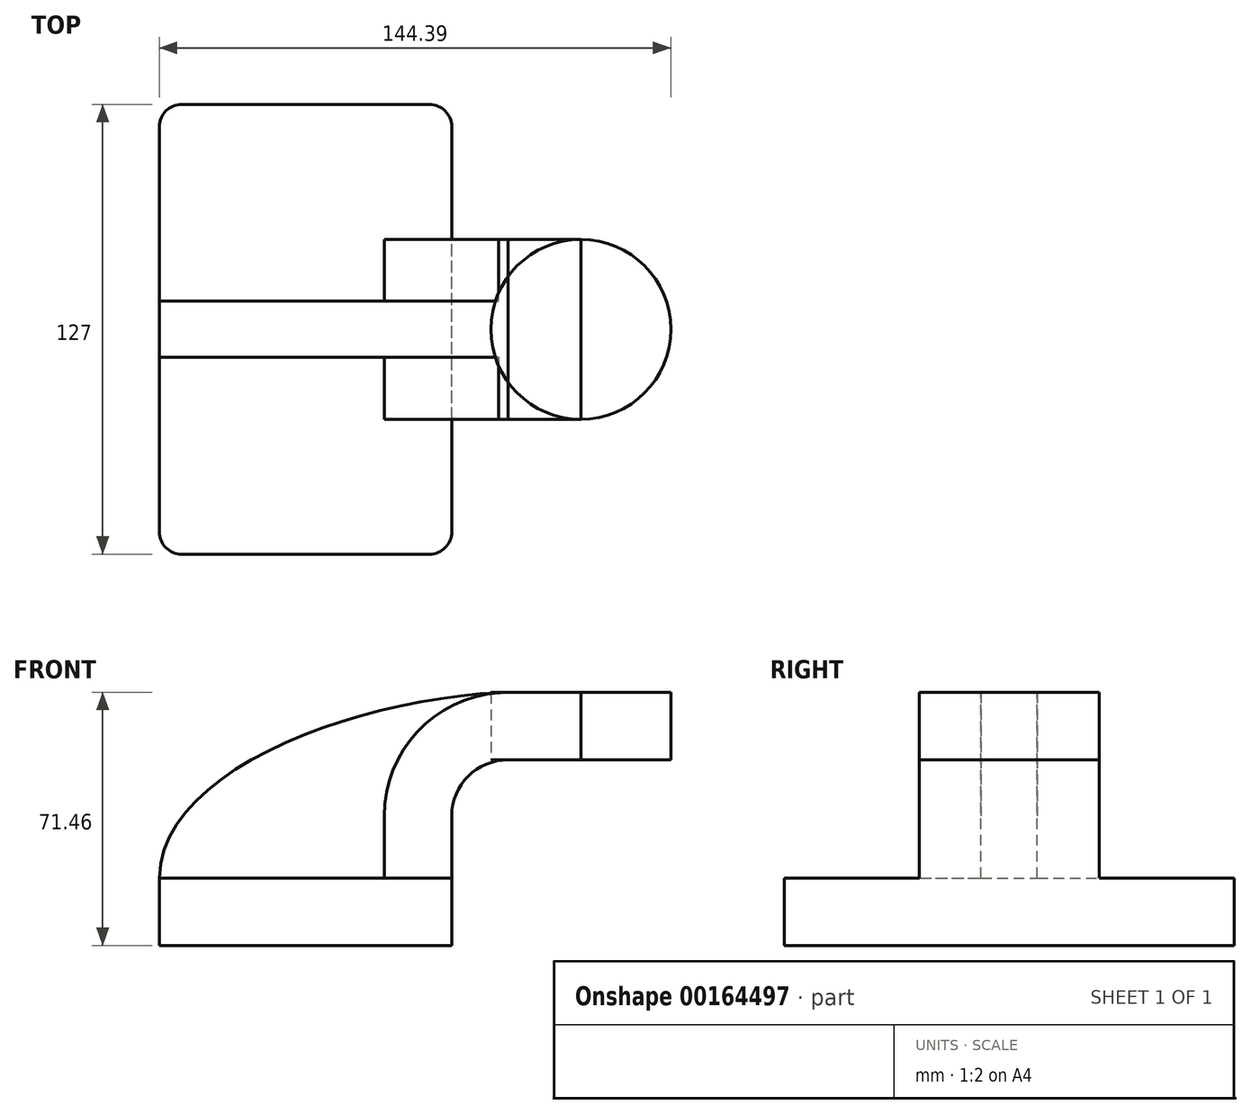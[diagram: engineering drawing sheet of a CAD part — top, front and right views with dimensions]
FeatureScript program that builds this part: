
annotation { "Feature Type Name" : "Feature", "Feature Type Description" : "" }
export const myFeature = defineFeature(function(context is Context, id is Id, definition is map)
    precondition{}
    {
        {
            var Q0;
            Q0=qCreatedBy(makeId("Front.planeOp"),FACE);
            var sketch = newSketch(context, id + "F0", { "sketchPlane" : qUnion([Q0])});
            skLineSegment(sketch, "E0.bottom", {"start": v(41.28, -9.52) * mm, "end": v(-41.28, -9.53) * mm});
            skLineSegment(sketch, "E0.top", {"start": v(41.28, 9.53) * mm, "end": v(-41.28, 9.53) * mm});
            skLineSegment(sketch, "E0.left", {"start": v(41.28, -9.52) * mm, "end": v(41.28, 9.53) * mm});
            skLineSegment(sketch, "E0.right", {"start": v(-41.28, -9.53) * mm, "end": v(-41.28, 9.53) * mm});
            skPoint(sketch, "E0.middle", {"position": v(0, 0) * mm});
            skLineSegment(sketch, "E1.bottom", {"start": v(128.51, 38.1) * mm, "end": v(77.71, 38.1) * mm});
            skLineSegment(sketch, "E1.top", {"start": v(128.51, 66.68) * mm, "end": v(77.71, 66.68) * mm});
            skLineSegment(sketch, "E1.left", {"start": v(128.51, 38.1) * mm, "end": v(128.51, 66.68) * mm});
            skLineSegment(sketch, "E1.right", {"start": v(77.71, 38.1) * mm, "end": v(77.71, 66.68) * mm});
            skPoint(sketch, "E1.middle", {"position": v(103.11, 52.39) * mm});
            skLineSegment(sketch, "E2", {"start": v(41.28, 9.53) * mm, "end": v(41.28, 27) * mm});
            skArc(sketch, "E3", {"start": v(41.27, 27) * mm, "mid": v(45.92, 38.23) * mm, "end": v(57.15, 42.88) * mm});
            skLineSegment(sketch, "E4", {"start": v(57.15, 42.88) * mm, "end": v(103.11, 42.88) * mm});
            skPoint(sketch, "E4.endSnap0", {"position": v(103.11, 38.1) * mm});
            skLineSegment(sketch, "E5.0", {"start": v(57.15, 61.93) * mm, "end": v(103.11, 61.93) * mm});
            skArc(sketch, "E5.1", {"start": v(22.23, 27) * mm, "mid": v(32.45, 51.7) * mm, "end": v(57.15, 61.93) * mm});
            skLineSegment(sketch, "E5.2", {"start": v(22.22, 9.53) * mm, "end": v(22.22, 27) * mm});
            skLineSegment(sketch, "E6", {"start": v(103.11, 42.88) * mm, "end": v(103.11, 61.93) * mm});
            skFitSpline(sketch, "E7", {"points": [v(-41.28, 9.53) * mm, v(57.15, 61.93) * mm], "startDerivative": vector(1.48, 94.5) * mm, "endDerivative": vector(120.77, 3.4) * mm});
            skSolve(sketch);
        }
        {
            var Q0;
            Q0=makeQuery(id+"F0.imprint","IMPRINT",FACE,{"disambiguationData":[TD([[makeQuery(id+"F0.imprint","IMPRINT",EDGE,{"derivedFrom":sQuery(id+"F0.wireOp",EDGE,"E0.bottom")}),-1.0]])]});
            extrude(context, id + "F1", {"entities" : qUnion([Q0]), "endBound" : BoundingType.SYMMETRIC, "depth" : 127 * mm});
        }
        {
            var Q0;
            {var subQ1=sQuery(id+"F0.wireOp",EDGE,"E2");Q0=makeQuery(id+"F0.imprint","IMPRINT",FACE,{"disambiguationData":[TD([[makeQuery(id+"F0.imprint","IMPRINT",EDGE,{"derivedFrom":subQ1}),1.0]])]});}
            extrude(context, id + "F2", {"entities" : qUnion([Q0]), "operationType" : NewBodyOperationType.ADD, "endBound" : BoundingType.SYMMETRIC, "depth" : 50.8 * mm});
        }
        {
            var Q0;
            {var subQ3=sQuery(id+"F0.wireOp",EDGE,"E5.2");Q0=makeQuery(id+"F0.imprint","IMPRINT",FACE,{"disambiguationData":[TD([[makeQuery(id+"F0.imprint","IMPRINT",EDGE,{"derivedFrom":subQ3}),1.0]])]});}
            extrude(context, id + "F3", {"entities" : qUnion([Q0]), "operationType" : NewBodyOperationType.ADD, "endBound" : BoundingType.SYMMETRIC, "depth" : 15.88 * mm});
        }
        {
            var Q0;
            {var subQ5=sQuery(id+"F0.wireOp",EDGE,"E6");Q0=makeQuery(id+"F0.imprint","IMPRINT",FACE,{"disambiguationData":[TD([[makeQuery(id+"F0.imprint","IMPRINT",EDGE,{"derivedFrom":subQ5}),1.0]])]});}
            var Q1;
            Q1=sQuery(id+"F0.wireOp",EDGE,"E1.right");
            revolve(context, id + "F4", {"entities" : qUnion([Q0]), "axis" : qUnion([Q1]), "revolveType" : RevolveType.FULL});
        }
        {
            var Q0;
            Q0=makeQuery(id+"F1.opExtrude","CAP_EDGE",EDGE,{"disambiguationData":[OSD([sQuery(id+"F0.wireOp",EDGE,"E0.left")])],"isStart":false});
            var Q1;
            Q1=makeQuery(id+"F1.opExtrude","CAP_EDGE",EDGE,{"disambiguationData":[OSD([sQuery(id+"F0.wireOp",EDGE,"E0.right")])],"isStart":false});
            var Q2;
            Q2=makeQuery(id+"F1.opExtrude","CAP_EDGE",EDGE,{"disambiguationData":[OSD([sQuery(id+"F0.wireOp",EDGE,"E0.left")])],"isStart":true});
            var Q3;
            Q3=makeQuery(id+"F1.opExtrude","CAP_EDGE",EDGE,{"disambiguationData":[OSD([sQuery(id+"F0.wireOp",EDGE,"E0.right")])],"isStart":true});
            fillet(context, id + "F5", {"entities" : qUnion([Q0, Q1, Q2, Q3]), "radius" : 6.35 * mm, "tangentPropagation" : true, "allowEdgeOverflow" : false});
        }
    });
